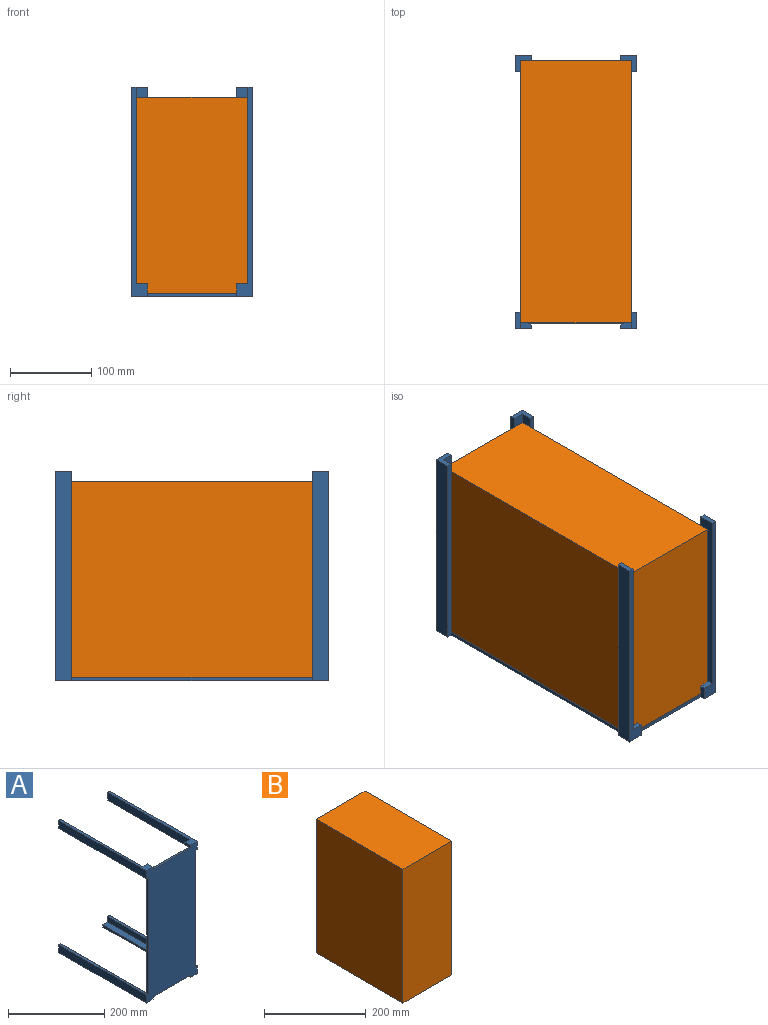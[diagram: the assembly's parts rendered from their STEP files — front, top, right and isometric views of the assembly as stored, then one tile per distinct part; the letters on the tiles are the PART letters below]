
ASSEMBLY  parts=2 mates=1
PART A: 46 faces, bbox 149.9x257.5x336.6 mm
  f0: plane 14x12mm, normal (0,0,-1), area 148mm2, adj f4,f6,f19,f39,f40,f41
  f1: plane 14x12mm, normal (0,0,-1), area 148mm2, adj f5,f7,f19,f36,f37,f38
  f2: plane 257.48x20mm, normal (0,0,1), area 1768.9mm2, adj f4,f6,f13,f18,f41,f43
  f3: plane 257.48x20mm, normal (0,0,1), area 1768.9mm2, adj f5,f7,f12,f13,f38,f42
  f4: plane 16x6mm, normal (1,0,0), area 96mm2, adj f0,f2,f13,f23,f41
  f5: plane 16x6mm, normal (-1,0,0), area 96mm2, adj f1,f3,f13,f23,f38
  f6: plane 253.48x20mm, normal (1,0,0), area 4977.6mm2, adj f0,f2,f19,f26,f39,f40,f41,f43
  f7: plane 253.48x20mm, normal (-1,0,0), area 4977.6mm2, adj f1,f3,f19,f29,f36,f37,f38,f42
  f8: plane 253.48x14mm, normal (0,0,1), area 3528.7mm2, adj f9,f19,f22,f33,f34,f35,f45
  f9: plane 253.48x14mm, normal (-1,0,0), area 3528.7mm2, adj f8,f19,f28,f33,f34,f35,f45
  f10: plane 253.48x14mm, normal (1,0,0), area 3528.7mm2, adj f11,f19,f25,f30,f31,f32,f44
  f11: plane 253.48x14mm, normal (0,0,1), area 3528.7mm2, adj f10,f19,f21,f30,f31,f32,f44
  f12: plane 257.48x20mm, normal (1,0,0), area 5149.6mm2, adj f3,f13,f29,f42
  f13: plane 336.6x149.9mm, normal (0,-1,0), area 45578.3mm2, adj f2,f3,f4,f5,f12,f14,f15,f16
  f14: plane 257.48x20mm, normal (-1,0,0), area 5149.6mm2, adj f13,f17,f25,f44
  f15: plane 257.48x20mm, normal (0,0,-1), area 5149.6mm2, adj f13,f16,f22,f45
  f16: plane 257.48x20mm, normal (1,0,0), area 5149.6mm2, adj f13,f15,f28,f45
  f17: plane 257.48x20mm, normal (0,0,-1), area 5149.6mm2, adj f13,f14,f21,f44
  f18: plane 257.48x20mm, normal (-1,0,0), area 5149.6mm2, adj f2,f13,f26,f43
  f19: plane 324.6x137.9mm, normal (0,1,0), area 44762.3mm2, adj f0,f1,f6,f7,f8,f9,f10,f11
  f20: plane 109.9x4mm, normal (0,0,-1), area 439.6mm2, adj f13,f19,f21,f22
  f21: plane 257.48x6mm, normal (1,0,0), area 1544.9mm2, adj f11,f13,f17,f20,f44
  f22: plane 257.48x6mm, normal (-1,0,0), area 1544.9mm2, adj f8,f13,f15,f20,f45
  f23: plane 109.9x4mm, normal (0,0,1), area 439.6mm2, adj f4,f5,f13,f19
  f24: plane 296.6x4mm, normal (-1,0,0), area 1186.4mm2, adj f13,f19,f25,f26
  f25: plane 257.48x6mm, normal (0,0,1), area 1544.9mm2, adj f10,f13,f14,f24,f44
  f26: plane 257.48x6mm, normal (0,0,-1), area 1544.9mm2, adj f6,f13,f18,f24,f43
  f27: plane 296.6x4mm, normal (1,0,0), area 1186.4mm2, adj f13,f19,f28,f29
  f28: plane 257.48x6mm, normal (0,0,1), area 1544.9mm2, adj f9,f13,f16,f27,f45
  f29: plane 257.48x6mm, normal (0,0,-1), area 1544.9mm2, adj f7,f12,f13,f27,f42
  f30: plane 10x10mm, normal (0.71,0,0.71), area 28.3mm2, adj f10,f11,f31,f32
  f31: plane 10x10mm, normal (0,-1,0), area 50mm2, adj f10,f11,f30
  f32: plane 10x10mm, normal (0,1,0), area 50mm2, adj f10,f11,f30
  f33: plane 10x10mm, normal (-0.71,0,0.71), area 28.3mm2, adj f8,f9,f34,f35
  f34: plane 10x10mm, normal (0,-1,0), area 50mm2, adj f8,f9,f33
  f35: plane 10x10mm, normal (0,1,0), area 50mm2, adj f8,f9,f33
  f36: plane 10x10mm, normal (-0.71,0,-0.71), area 28.3mm2, adj f1,f7,f37,f38
  f37: plane 10x10mm, normal (0,-1,0), area 50mm2, adj f1,f7,f36
  f38: plane 16x14mm, normal (0,1,0), area 134mm2, adj f1,f3,f5,f7,f36
  f39: plane 10x10mm, normal (0.71,0,-0.71), area 28.3mm2, adj f0,f6,f40,f41
  f40: plane 10x10mm, normal (0,-1,0), area 50mm2, adj f0,f6,f39
  f41: plane 16x14mm, normal (0,1,0), area 134mm2, adj f0,f2,f4,f6,f39
  f42: plane 20x6mm, normal (0,1,0), area 120mm2, adj f3,f7,f12,f29
  f43: plane 20x6mm, normal (0,1,0), area 120mm2, adj f2,f6,f18,f26
  f44: plane 20x20mm, normal (0,1,0), area 204mm2, adj f10,f11,f14,f17,f21,f25
  f45: plane 20x20mm, normal (0,1,0), area 204mm2, adj f8,f9,f15,f16,f22,f28
PART B: 6 faces, bbox 135.9x241.6x322.6 mm
  f0: plane 322.6x241.62mm, normal (1,0,0), area 77946.6mm2, adj f1,f3,f4,f5
  f1: plane 241.62x135.9mm, normal (0,0,-1), area 32836.2mm2, adj f0,f2,f4,f5
  f2: plane 322.6x241.62mm, normal (-1,0,0), area 77946.6mm2, adj f1,f3,f4,f5
  f3: plane 241.62x135.9mm, normal (0,0,1), area 32836.2mm2, adj f0,f2,f4,f5
  f4: plane 322.6x135.9mm, normal (0,-1,0), area 43841.3mm2, adj f0,f1,f2,f3
  f5: plane 322.6x135.9mm, normal (0,1,0), area 43841.3mm2, adj f0,f1,f2,f3
PLACE A rot(axis=(1,0,0),90deg) t=(0,0,4)mm
PLACE B rot(axis=(1,0,0),90deg) t=(0,0,4)mm
MATE fastened B.f4 <-> A.f19  axis (0,0,-1) through (0,0,4)mm
